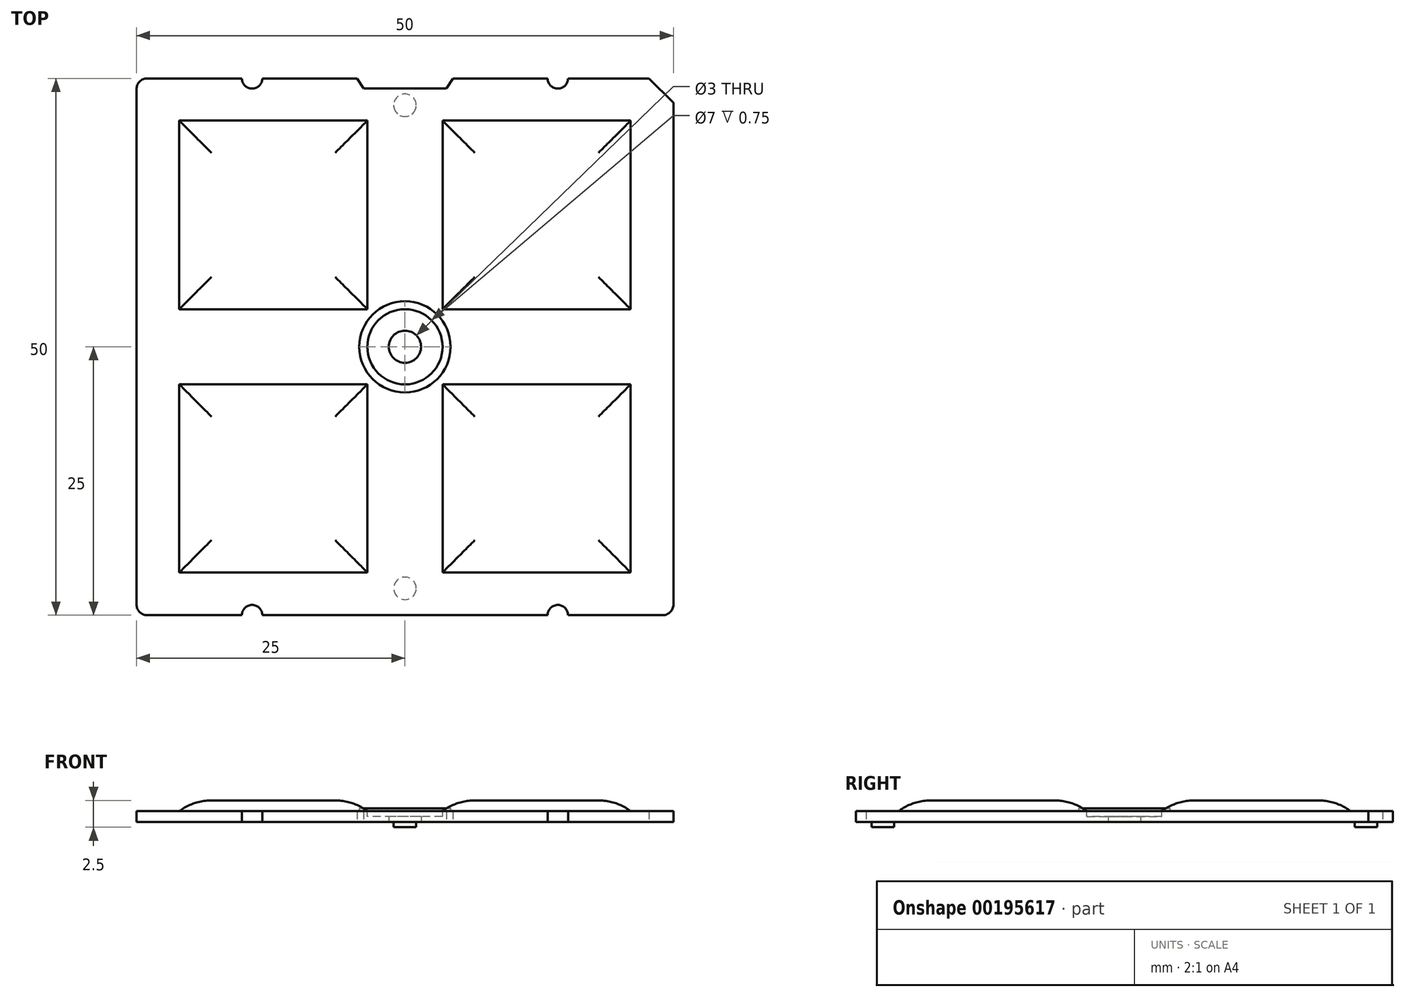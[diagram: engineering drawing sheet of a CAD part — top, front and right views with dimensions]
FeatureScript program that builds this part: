
annotation { "Feature Type Name" : "Feature", "Feature Type Description" : "" }
export const myFeature = defineFeature(function(context is Context, id is Id, definition is map)
    precondition{}
    {
        {
            var Q0;
            Q0=qCreatedBy(makeId("Top.planeOp"),FACE);
            var sketch = newSketch(context, id + "F0", { "sketchPlane" : qUnion([Q0])});
            skLineSegment(sketch, "E0.bottom", {"start": v(-24, -25) * mm, "end": v(-15.19, -25) * mm});
            skLineSegment(sketch, "E0.top", {"start": v(-24, 25) * mm, "end": v(-15.19, 25) * mm});
            skLineSegment(sketch, "E0.left", {"start": v(-25, -24) * mm, "end": v(-25, 24) * mm});
            skLineSegment(sketch, "E0.right", {"start": v(25, -24) * mm, "end": v(25, 22.72) * mm});
            skPoint(sketch, "E0.middle", {"position": v(0, 0) * mm});
            skLineSegment(sketch, "E1.bottom", {"start": v(-21.02, -21.02) * mm, "end": v(-3.5, -21.02) * mm});
            skLineSegment(sketch, "E1.top", {"start": v(-21.02, -3.5) * mm, "end": v(-3.5, -3.5) * mm});
            skLineSegment(sketch, "E1.left", {"start": v(-21.02, -21.02) * mm, "end": v(-21.02, -3.5) * mm});
            skLineSegment(sketch, "E1.right", {"start": v(-3.5, -21.02) * mm, "end": v(-3.5, -3.5) * mm});
            skPoint(sketch, "E1.middle", {"position": v(-12.26, -12.26) * mm});
            skLineSegment(sketch, "E2.bottom", {"start": v(-21.02, 3.5) * mm, "end": v(-3.5, 3.5) * mm});
            skLineSegment(sketch, "E2.top", {"start": v(-21.02, 21.07) * mm, "end": v(-3.5, 21.07) * mm});
            skLineSegment(sketch, "E2.left", {"start": v(-21.02, 3.5) * mm, "end": v(-21.02, 21.07) * mm});
            skLineSegment(sketch, "E2.right", {"start": v(-3.5, 3.5) * mm, "end": v(-3.5, 21.07) * mm});
            skPoint(sketch, "E2.middle", {"position": v(-12.26, 12.29) * mm});
            skPoint(sketch, "E2.middle.positionSnap0", {"position": v(-12.26, -3.5) * mm});
            skPoint(sketch, "E2.centerSnap0", {"position": v(-12.26, -3.5) * mm});
            skLineSegment(sketch, "E3.MirrorCS", {"start": v(21.02, 21.07) * mm, "end": v(3.5, 21.07) * mm});
            skLineSegment(sketch, "E4.MirrorCS", {"start": v(21.02, 3.5) * mm, "end": v(21.02, 21.07) * mm});
            skLineSegment(sketch, "E5.MirrorCS", {"start": v(3.5, 3.5) * mm, "end": v(3.5, 21.07) * mm});
            skLineSegment(sketch, "E6.MirrorCS", {"start": v(21.02, 3.5) * mm, "end": v(3.5, 3.5) * mm});
            skLineSegment(sketch, "E7.MirrorCS", {"start": v(21.02, -3.5) * mm, "end": v(3.5, -3.5) * mm});
            skLineSegment(sketch, "E8.MirrorCS", {"start": v(3.5, -21.02) * mm, "end": v(3.5, -3.5) * mm});
            skLineSegment(sketch, "E9.MirrorCS", {"start": v(21.02, -21.02) * mm, "end": v(3.5, -21.02) * mm});
            skLineSegment(sketch, "E10", {"start": v(21.02, -3.5) * mm, "end": v(21.02, -21.02) * mm});
            skPoint(sketch, "E11.visualSharp", {"position": v(-25, 25) * mm});
            skArc(sketch, "E11.filletArc", {"start": v(-24, 25) * mm, "mid": v(-24.7, 24.7) * mm, "end": v(-25, 24) * mm});
            skPoint(sketch, "E12.visualSharp", {"position": v(-25, -25) * mm});
            skArc(sketch, "E12.filletArc", {"start": v(-25, -24) * mm, "mid": v(-24.7, -24.7) * mm, "end": v(-24, -25) * mm});
            skPoint(sketch, "E13.visualSharp", {"position": v(25, -25) * mm});
            skArc(sketch, "E13.filletArc", {"start": v(24, -25) * mm, "mid": v(24.7, -24.7) * mm, "end": v(25, -24) * mm});
            skLineSegment(sketch, "E14", {"start": v(22.72, 25) * mm, "end": v(25, 22.72) * mm});
            skPoint(sketch, "E15.orphan", {"position": v(25, 25) * mm});
            skCircle(sketch, "E16", {"center": v(0, 0) * mm, "radius": 1.5 * mm});
            skLineSegment(sketch, "E17", {"start": v(-4.47, 25) * mm, "end": v(-3.87, 24.05) * mm});
            skLineSegment(sketch, "E18", {"start": v(-3.87, 24.05) * mm, "end": v(0, 24.05) * mm});
            skLineSegment(sketch, "E19.MirrorCS", {"start": v(3.87, 24.05) * mm, "end": v(0, 24.05) * mm});
            skLineSegment(sketch, "E20.MirrorCS", {"start": v(4.47, 25) * mm, "end": v(3.87, 24.05) * mm});
            skLineSegment(sketch, "E21.trimOffspring", {"start": v(4.47, 25) * mm, "end": v(13.28, 25) * mm});
            skArc(sketch, "E22", {"start": v(-15.19, 25) * mm, "mid": v(-14.24, 24.05) * mm, "end": v(-13.28, 25) * mm});
            skLineSegment(sketch, "E23.trimOffspring", {"start": v(-13.28, 25) * mm, "end": v(-4.47, 25) * mm});
            skPoint(sketch, "E24.center.orphan", {"position": v(0, 25) * mm});
            skArc(sketch, "E25.MirrorCS", {"start": v(15.19, 25) * mm, "mid": v(14.24, 24.05) * mm, "end": v(13.28, 25) * mm});
            skLineSegment(sketch, "E26.trimOffspring", {"start": v(15.19, 25) * mm, "end": v(22.72, 25) * mm});
            skArc(sketch, "E27.MirrorCS", {"start": v(-15.19, -25) * mm, "mid": v(-14.24, -24.05) * mm, "end": v(-13.28, -25) * mm});
            skArc(sketch, "E28.MirrorCS", {"start": v(15.19, -25) * mm, "mid": v(14.24, -24.05) * mm, "end": v(13.28, -25) * mm});
            skLineSegment(sketch, "E29.trimOffspring", {"start": v(-13.28, -25) * mm, "end": v(13.28, -25) * mm});
            skLineSegment(sketch, "E30.trimOffspring", {"start": v(15.19, -25) * mm, "end": v(24, -25) * mm});
            skSolve(sketch);
        }
        {
            var Q0;
            Q0 = qSketchRegion(id + "F0", true);
            extrude(context, id + "F1", {"entities" : qUnion([Q0]), "depth" : 1 * mm});
        }
        {
            var Q0;
            Q0=makeQuery(id+"F1.opExtrude","CAP_FACE",FACE,{"disambiguationData":[OSD([sQuery(id+"F0.wireOp",EDGE,"E0.bottom"),sQuery(id+"F0.wireOp",EDGE,"E0.top"),sQuery(id+"F0.wireOp",EDGE,"E0.left"),sQuery(id+"F0.wireOp",EDGE,"E0.right"),sQuery(id+"F0.wireOp",EDGE,"E1.bottom"),sQuery(id+"F0.wireOp",EDGE,"E1.top"),sQuery(id+"F0.wireOp",EDGE,"E1.left"),sQuery(id+"F0.wireOp",EDGE,"E1.right"),sQuery(id+"F0.wireOp",EDGE,"E2.bottom"),sQuery(id+"F0.wireOp",EDGE,"E2.top"),sQuery(id+"F0.wireOp",EDGE,"E2.left"),sQuery(id+"F0.wireOp",EDGE,"E2.right"),sQuery(id+"F0.wireOp",EDGE,"E3.MirrorCS"),sQuery(id+"F0.wireOp",EDGE,"E4.MirrorCS"),sQuery(id+"F0.wireOp",EDGE,"E5.MirrorCS"),sQuery(id+"F0.wireOp",EDGE,"E6.MirrorCS"),sQuery(id+"F0.wireOp",EDGE,"E7.MirrorCS"),sQuery(id+"F0.wireOp",EDGE,"E9.MirrorCS"),sQuery(id+"F0.wireOp",EDGE,"E8.MirrorCS"),sQuery(id+"F0.wireOp",EDGE,"E10"),sQuery(id+"F0.wireOp",EDGE,"E11.filletArc"),sQuery(id+"F0.wireOp",EDGE,"E12.filletArc"),sQuery(id+"F0.wireOp",EDGE,"E13.filletArc"),sQuery(id+"F0.wireOp",EDGE,"E14"),sQuery(id+"F0.wireOp",EDGE,"E16"),sQuery(id+"F0.wireOp",EDGE,"E17"),sQuery(id+"F0.wireOp",EDGE,"E18"),sQuery(id+"F0.wireOp",EDGE,"E19.MirrorCS"),sQuery(id+"F0.wireOp",EDGE,"E20.MirrorCS"),sQuery(id+"F0.wireOp",EDGE,"E21.trimOffspring"),sQuery(id+"F0.wireOp",EDGE,"E22"),sQuery(id+"F0.wireOp",EDGE,"E23.trimOffspring"),sQuery(id+"F0.wireOp",EDGE,"E25.MirrorCS"),sQuery(id+"F0.wireOp",EDGE,"E26.trimOffspring"),sQuery(id+"F0.wireOp",EDGE,"E27.MirrorCS"),sQuery(id+"F0.wireOp",EDGE,"E28.MirrorCS"),sQuery(id+"F0.wireOp",EDGE,"E29.trimOffspring"),sQuery(id+"F0.wireOp",EDGE,"E30.trimOffspring")])],"isStart":false});
            var sketch = newSketch(context, id + "F2", { "sketchPlane" : qUnion([Q0])});
            skSolve(sketch);
        }
        {
            var Q0;
            Q0=makeQuery(id+"F2.imprint","IMPRINT",FACE,{"disambiguationData":[TD([[makeQuery(id+"F2.imprint","IMPRINT",EDGE,{"derivedFrom":makeQuery(id+"F1.opExtrude","CAP_EDGE",EDGE,{"disambiguationData":[OSD([sQuery(id+"F0.wireOp",EDGE,"E2.bottom")])],"isStart":false})}),1.0]])]});
            var Q1;
            Q1=makeQuery(id+"F2.imprint","IMPRINT",FACE,{"disambiguationData":[TD([[makeQuery(id+"F2.imprint","IMPRINT",EDGE,{"derivedFrom":makeQuery(id+"F1.opExtrude","CAP_EDGE",EDGE,{"disambiguationData":[OSD([sQuery(id+"F0.wireOp",EDGE,"E3.MirrorCS")])],"isStart":false})}),1.0]])]});
            var Q2;
            Q2=makeQuery(id+"F2.imprint","IMPRINT",FACE,{"disambiguationData":[TD([[makeQuery(id+"F2.imprint","IMPRINT",EDGE,{"derivedFrom":makeQuery(id+"F1.opExtrude","CAP_EDGE",EDGE,{"disambiguationData":[OSD([sQuery(id+"F0.wireOp",EDGE,"E7.MirrorCS")])],"isStart":false})}),1.0]])]});
            var Q3;
            Q3=makeQuery(id+"F2.imprint","IMPRINT",FACE,{"disambiguationData":[TD([[makeQuery(id+"F2.imprint","IMPRINT",EDGE,{"derivedFrom":makeQuery(id+"F1.opExtrude","CAP_EDGE",EDGE,{"disambiguationData":[OSD([sQuery(id+"F0.wireOp",EDGE,"E1.bottom")])],"isStart":false})}),1.0]])]});
            extrude(context, id + "F3", {"entities" : qUnion([Q0, Q1, Q2, Q3]), "operationType" : NewBodyOperationType.ADD, "endBound" : BoundingType.SYMMETRIC, "depth" : 2 * mm});
        }
        {
            var Q0;
            Q0=makeQuery(id+"F1.opExtrude","CAP_FACE",FACE,{"disambiguationData":[OSD([sQuery(id+"F0.wireOp",EDGE,"E0.bottom"),sQuery(id+"F0.wireOp",EDGE,"E0.top"),sQuery(id+"F0.wireOp",EDGE,"E0.left"),sQuery(id+"F0.wireOp",EDGE,"E0.right"),sQuery(id+"F0.wireOp",EDGE,"E1.bottom"),sQuery(id+"F0.wireOp",EDGE,"E1.top"),sQuery(id+"F0.wireOp",EDGE,"E1.left"),sQuery(id+"F0.wireOp",EDGE,"E1.right"),sQuery(id+"F0.wireOp",EDGE,"E2.bottom"),sQuery(id+"F0.wireOp",EDGE,"E2.top"),sQuery(id+"F0.wireOp",EDGE,"E2.left"),sQuery(id+"F0.wireOp",EDGE,"E2.right"),sQuery(id+"F0.wireOp",EDGE,"E3.MirrorCS"),sQuery(id+"F0.wireOp",EDGE,"E4.MirrorCS"),sQuery(id+"F0.wireOp",EDGE,"E5.MirrorCS"),sQuery(id+"F0.wireOp",EDGE,"E6.MirrorCS"),sQuery(id+"F0.wireOp",EDGE,"E7.MirrorCS"),sQuery(id+"F0.wireOp",EDGE,"E9.MirrorCS"),sQuery(id+"F0.wireOp",EDGE,"E8.MirrorCS"),sQuery(id+"F0.wireOp",EDGE,"E10"),sQuery(id+"F0.wireOp",EDGE,"E11.filletArc"),sQuery(id+"F0.wireOp",EDGE,"E12.filletArc"),sQuery(id+"F0.wireOp",EDGE,"E13.filletArc"),sQuery(id+"F0.wireOp",EDGE,"E14"),sQuery(id+"F0.wireOp",EDGE,"E16"),sQuery(id+"F0.wireOp",EDGE,"E17"),sQuery(id+"F0.wireOp",EDGE,"E18"),sQuery(id+"F0.wireOp",EDGE,"E19.MirrorCS"),sQuery(id+"F0.wireOp",EDGE,"E20.MirrorCS"),sQuery(id+"F0.wireOp",EDGE,"E21.trimOffspring"),sQuery(id+"F0.wireOp",EDGE,"E22"),sQuery(id+"F0.wireOp",EDGE,"E23.trimOffspring"),sQuery(id+"F0.wireOp",EDGE,"E25.MirrorCS"),sQuery(id+"F0.wireOp",EDGE,"E26.trimOffspring"),sQuery(id+"F0.wireOp",EDGE,"E27.MirrorCS"),sQuery(id+"F0.wireOp",EDGE,"E28.MirrorCS"),sQuery(id+"F0.wireOp",EDGE,"E29.trimOffspring"),sQuery(id+"F0.wireOp",EDGE,"E30.trimOffspring")])],"isStart":false});
            var sketch = newSketch(context, id + "F4", { "sketchPlane" : qUnion([Q0])});
            skCircle(sketch, "E31", {"center": v(0, 0) * mm, "radius": 3.5 * mm});
            skSolve(sketch);
        }
        {
            var Q0;
            Q0 = qSketchRegion(id + "F4", true);
            extrude(context, id + "F5", {"entities" : qUnion([Q0]), "operationType" : NewBodyOperationType.REMOVE, "oppositeDirection" : true, "depth" : .5 * mm});
        }
        {
            var Q0;
            Q0=makeQuery(id+"F1.opExtrude","CAP_FACE",FACE,{"disambiguationData":[OSD([sQuery(id+"F0.wireOp",EDGE,"E0.bottom"),sQuery(id+"F0.wireOp",EDGE,"E0.top"),sQuery(id+"F0.wireOp",EDGE,"E0.left"),sQuery(id+"F0.wireOp",EDGE,"E0.right"),sQuery(id+"F0.wireOp",EDGE,"E1.bottom"),sQuery(id+"F0.wireOp",EDGE,"E1.top"),sQuery(id+"F0.wireOp",EDGE,"E1.left"),sQuery(id+"F0.wireOp",EDGE,"E1.right"),sQuery(id+"F0.wireOp",EDGE,"E2.bottom"),sQuery(id+"F0.wireOp",EDGE,"E2.top"),sQuery(id+"F0.wireOp",EDGE,"E2.left"),sQuery(id+"F0.wireOp",EDGE,"E2.right"),sQuery(id+"F0.wireOp",EDGE,"E3.MirrorCS"),sQuery(id+"F0.wireOp",EDGE,"E4.MirrorCS"),sQuery(id+"F0.wireOp",EDGE,"E5.MirrorCS"),sQuery(id+"F0.wireOp",EDGE,"E6.MirrorCS"),sQuery(id+"F0.wireOp",EDGE,"E7.MirrorCS"),sQuery(id+"F0.wireOp",EDGE,"E9.MirrorCS"),sQuery(id+"F0.wireOp",EDGE,"E8.MirrorCS"),sQuery(id+"F0.wireOp",EDGE,"E10"),sQuery(id+"F0.wireOp",EDGE,"E11.filletArc"),sQuery(id+"F0.wireOp",EDGE,"E12.filletArc"),sQuery(id+"F0.wireOp",EDGE,"E13.filletArc"),sQuery(id+"F0.wireOp",EDGE,"E14"),sQuery(id+"F0.wireOp",EDGE,"E16"),sQuery(id+"F0.wireOp",EDGE,"E17"),sQuery(id+"F0.wireOp",EDGE,"E18"),sQuery(id+"F0.wireOp",EDGE,"E19.MirrorCS"),sQuery(id+"F0.wireOp",EDGE,"E20.MirrorCS"),sQuery(id+"F0.wireOp",EDGE,"E21.trimOffspring"),sQuery(id+"F0.wireOp",EDGE,"E22"),sQuery(id+"F0.wireOp",EDGE,"E23.trimOffspring"),sQuery(id+"F0.wireOp",EDGE,"E25.MirrorCS"),sQuery(id+"F0.wireOp",EDGE,"E26.trimOffspring"),sQuery(id+"F0.wireOp",EDGE,"E27.MirrorCS"),sQuery(id+"F0.wireOp",EDGE,"E28.MirrorCS"),sQuery(id+"F0.wireOp",EDGE,"E29.trimOffspring"),sQuery(id+"F0.wireOp",EDGE,"E30.trimOffspring")])],"isStart":false});
            var sketch = newSketch(context, id + "F6", { "sketchPlane" : qUnion([Q0])});
            skCircle(sketch, "E32.0", {"center": v(0, 0) * mm, "radius": 3.5 * mm});
            skCircle(sketch, "E33.0", {"center": v(0, 0) * mm, "radius": 4.25 * mm});
            skSolve(sketch);
        }
        {
            var Q0;
            Q0 = qSketchRegion(id + "F6", true);
            extrude(context, id + "F7", {"entities" : qUnion([Q0]), "operationType" : NewBodyOperationType.ADD, "depth" : .25 * mm});
        }
        {
            var Q0;
            Q0=makeQuery(id+"F3.opExtrude","CAP_FACE",FACE,{"disambiguationData":[OSD([sQuery(id+"F0.wireOp",EDGE,"E1.bottom"),sQuery(id+"F0.wireOp",EDGE,"E1.top"),sQuery(id+"F0.wireOp",EDGE,"E1.left"),sQuery(id+"F0.wireOp",EDGE,"E1.right")])],"isStart":false});
            var Q1;
            Q1=makeQuery(id+"F3.opExtrude","CAP_FACE",FACE,{"disambiguationData":[OSD([sQuery(id+"F0.wireOp",EDGE,"E2.bottom"),sQuery(id+"F0.wireOp",EDGE,"E2.top"),sQuery(id+"F0.wireOp",EDGE,"E2.left"),sQuery(id+"F0.wireOp",EDGE,"E2.right")])],"isStart":false});
            var Q2;
            Q2=makeQuery(id+"F3.opExtrude","CAP_FACE",FACE,{"disambiguationData":[OSD([sQuery(id+"F0.wireOp",EDGE,"E3.MirrorCS"),sQuery(id+"F0.wireOp",EDGE,"E4.MirrorCS"),sQuery(id+"F0.wireOp",EDGE,"E5.MirrorCS"),sQuery(id+"F0.wireOp",EDGE,"E6.MirrorCS")])],"isStart":false});
            var Q3;
            Q3=makeQuery(id+"F3.opExtrude","CAP_FACE",FACE,{"disambiguationData":[OSD([sQuery(id+"F0.wireOp",EDGE,"E7.MirrorCS"),sQuery(id+"F0.wireOp",EDGE,"E9.MirrorCS"),sQuery(id+"F0.wireOp",EDGE,"E8.MirrorCS"),sQuery(id+"F0.wireOp",EDGE,"E10")])],"isStart":false});
            fillet(context, id + "F8", {"entities" : qUnion([Q0, Q1, Q2, Q3]), "radius" : 5 * mm, "tangentPropagation" : true, "allowEdgeOverflow" : false});
        }
        {
            var Q0;
            {var subQ0=sQuery(id+"F0.wireOp",EDGE,"E10");var subQ1=sQuery(id+"F0.wireOp",EDGE,"E8.MirrorCS");var subQ2=sQuery(id+"F0.wireOp",EDGE,"E9.MirrorCS");var subQ3=sQuery(id+"F0.wireOp",EDGE,"E7.MirrorCS");var subQ4=sQuery(id+"F0.wireOp",EDGE,"E6.MirrorCS");var subQ5=sQuery(id+"F0.wireOp",EDGE,"E5.MirrorCS");var subQ6=sQuery(id+"F0.wireOp",EDGE,"E4.MirrorCS");var subQ7=sQuery(id+"F0.wireOp",EDGE,"E3.MirrorCS");var subQ8=sQuery(id+"F0.wireOp",EDGE,"E2.right");var subQ9=sQuery(id+"F0.wireOp",EDGE,"E2.left");var subQ10=sQuery(id+"F0.wireOp",EDGE,"E2.top");var subQ11=sQuery(id+"F0.wireOp",EDGE,"E2.bottom");var subQ12=sQuery(id+"F0.wireOp",EDGE,"E1.right");var subQ13=sQuery(id+"F0.wireOp",EDGE,"E1.left");var subQ14=sQuery(id+"F0.wireOp",EDGE,"E1.top");var subQ15=sQuery(id+"F0.wireOp",EDGE,"E1.bottom");Q0=makeQuery(id+"F3.boolean.opBoolean","MERGE",FACE,{"derivedFrom":[makeQuery(id+"F1.opExtrude","CAP_FACE",FACE,{"disambiguationData":[OSD([sQuery(id+"F0.wireOp",EDGE,"E0.bottom"),sQuery(id+"F0.wireOp",EDGE,"E0.top"),sQuery(id+"F0.wireOp",EDGE,"E0.left"),sQuery(id+"F0.wireOp",EDGE,"E0.right"),subQ15,subQ14,subQ13,subQ12,subQ11,subQ10,subQ9,subQ8,subQ7,subQ6,subQ5,subQ4,subQ3,subQ2,subQ1,subQ0,sQuery(id+"F0.wireOp",EDGE,"E11.filletArc"),sQuery(id+"F0.wireOp",EDGE,"E12.filletArc"),sQuery(id+"F0.wireOp",EDGE,"E13.filletArc"),sQuery(id+"F0.wireOp",EDGE,"E14"),sQuery(id+"F0.wireOp",EDGE,"E16"),sQuery(id+"F0.wireOp",EDGE,"E17"),sQuery(id+"F0.wireOp",EDGE,"E18"),sQuery(id+"F0.wireOp",EDGE,"E19.MirrorCS"),sQuery(id+"F0.wireOp",EDGE,"E20.MirrorCS"),sQuery(id+"F0.wireOp",EDGE,"E21.trimOffspring"),sQuery(id+"F0.wireOp",EDGE,"E22"),sQuery(id+"F0.wireOp",EDGE,"E23.trimOffspring"),sQuery(id+"F0.wireOp",EDGE,"E25.MirrorCS"),sQuery(id+"F0.wireOp",EDGE,"E26.trimOffspring"),sQuery(id+"F0.wireOp",EDGE,"E27.MirrorCS"),sQuery(id+"F0.wireOp",EDGE,"E28.MirrorCS"),sQuery(id+"F0.wireOp",EDGE,"E29.trimOffspring"),sQuery(id+"F0.wireOp",EDGE,"E30.trimOffspring")])],"isStart":true}),makeQuery(id+"F3.opExtrude","CAP_FACE",FACE,{"disambiguationData":[OSD([subQ15,subQ14,subQ13,subQ12])],"isStart":true}),makeQuery(id+"F3.opExtrude","CAP_FACE",FACE,{"disambiguationData":[OSD([subQ11,subQ10,subQ9,subQ8])],"isStart":true}),makeQuery(id+"F3.opExtrude","CAP_FACE",FACE,{"disambiguationData":[OSD([subQ7,subQ6,subQ5,subQ4])],"isStart":true}),makeQuery(id+"F3.opExtrude","CAP_FACE",FACE,{"disambiguationData":[OSD([subQ3,subQ2,subQ1,subQ0])],"isStart":true})]});}
            var sketch = newSketch(context, id + "F9", { "sketchPlane" : qUnion([Q0])});
            skLineSegment(sketch, "E34", {"start": v(0, 25) * mm, "end": v(0, -24.05) * mm, "construction": true});
            skCircle(sketch, "E35", {"center": v(0, 22.5) * mm, "radius": 1.05 * mm});
            skCircle(sketch, "E36", {"center": v(0, -22.5) * mm, "radius": 1.05 * mm});
            skSolve(sketch);
        }
        {
            var Q0;
            Q0 = qSketchRegion(id + "F9", true);
            extrude(context, id + "F10", {"entities" : qUnion([Q0]), "operationType" : NewBodyOperationType.ADD, "depth" : .5 * mm});
        }
    });
